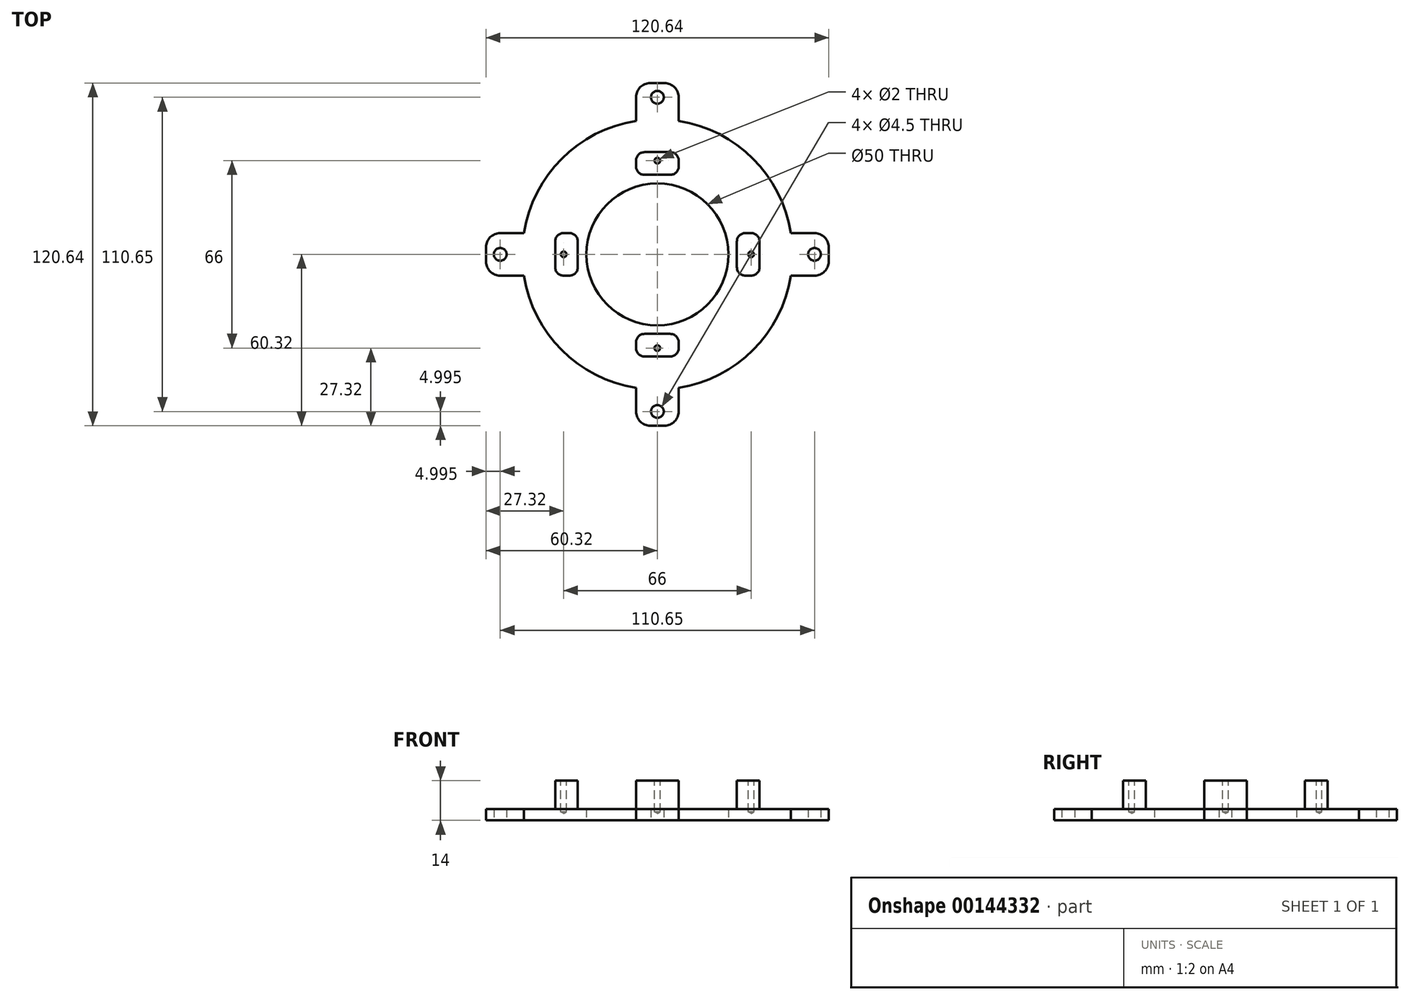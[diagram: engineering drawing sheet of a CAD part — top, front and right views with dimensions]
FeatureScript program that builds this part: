
annotation { "Feature Type Name" : "Feature", "Feature Type Description" : "" }
export const myFeature = defineFeature(function(context is Context, id is Id, definition is map)
    precondition{}
    {
        {
            var Q0;
            Q0=qCreatedBy(makeId("Top.planeOp"),FACE);
            var sketch = newSketch(context, id + "F0", { "sketchPlane" : qUnion([Q0])});
            skCircle(sketch, "E0", {"center": v(0, 0) * mm, "radius": 25 * mm});
            skCircle(sketch, "E1", {"center": v(0, 0) * mm, "radius": 47.63 * mm});
            skLineSegment(sketch, "E2", {"start": v(0, 47.63) * mm, "end": v(0, -47.63) * mm});
            skLineSegment(sketch, "E3", {"start": v(47.63, 0) * mm, "end": v(-47.63, 0) * mm});
            skLineSegment(sketch, "E4.bottom", {"start": v(7.5, 36) * mm, "end": v(-7.5, 36) * mm});
            skLineSegment(sketch, "E4.top", {"start": v(7.5, 28) * mm, "end": v(-7.5, 28) * mm});
            skLineSegment(sketch, "E4.left", {"start": v(7.5, 36) * mm, "end": v(7.5, 28) * mm});
            skLineSegment(sketch, "E4.right", {"start": v(-7.5, 36) * mm, "end": v(-7.5, 28) * mm});
            skPoint(sketch, "E5", {"position": v(0, 36) * mm});
            skPoint(sketch, "E6", {"position": v(0, 33) * mm});
            skLineSegment(sketch, "E7.bottom", {"start": v(-36, 7.5) * mm, "end": v(-28, 7.5) * mm});
            skLineSegment(sketch, "E7.top", {"start": v(-36, -7.5) * mm, "end": v(-28, -7.5) * mm});
            skLineSegment(sketch, "E7.left", {"start": v(-36, 7.5) * mm, "end": v(-36, -7.5) * mm});
            skLineSegment(sketch, "E7.right", {"start": v(-28, 7.5) * mm, "end": v(-28, -7.5) * mm});
            skLineSegment(sketch, "E8.bottom", {"start": v(36, 7.5) * mm, "end": v(28, 7.5) * mm});
            skLineSegment(sketch, "E8.top", {"start": v(36, -7.5) * mm, "end": v(28, -7.5) * mm});
            skLineSegment(sketch, "E8.left", {"start": v(36, 7.5) * mm, "end": v(36, -7.5) * mm});
            skLineSegment(sketch, "E8.right", {"start": v(28, 7.5) * mm, "end": v(28, -7.5) * mm});
            skLineSegment(sketch, "E9.bottom", {"start": v(7.5, -28) * mm, "end": v(-7.5, -28) * mm});
            skLineSegment(sketch, "E9.top", {"start": v(7.5, -36) * mm, "end": v(-7.5, -36) * mm});
            skLineSegment(sketch, "E9.left", {"start": v(7.5, -28) * mm, "end": v(7.5, -36) * mm});
            skLineSegment(sketch, "E9.right", {"start": v(-7.5, -28) * mm, "end": v(-7.5, -36) * mm});
            skPoint(sketch, "E10", {"position": v(36, 0) * mm});
            skPoint(sketch, "E11", {"position": v(-36, 0) * mm});
            skPoint(sketch, "E12", {"position": v(0, -36) * mm});
            skPoint(sketch, "E13", {"position": v(33, 0) * mm});
            skPoint(sketch, "E14", {"position": v(-33, 0) * mm});
            skPoint(sketch, "E15", {"position": v(0, -33) * mm});
            skLineSegment(sketch, "E16.bottom", {"start": v(-7.5, -36) * mm, "end": v(7.5, -36) * mm});
            skLineSegment(sketch, "E16.top", {"start": v(-7.5, -60.33) * mm, "end": v(7.5, -60.33) * mm});
            skLineSegment(sketch, "E16.left", {"start": v(-7.5, -36) * mm, "end": v(-7.5, -60.33) * mm});
            skLineSegment(sketch, "E16.right", {"start": v(7.5, -36) * mm, "end": v(7.5, -60.33) * mm});
            skLineSegment(sketch, "E17.bottom", {"start": v(-36, 7.5) * mm, "end": v(-60.33, 7.5) * mm});
            skLineSegment(sketch, "E17.top", {"start": v(-36, -7.5) * mm, "end": v(-60.33, -7.5) * mm});
            skLineSegment(sketch, "E17.right", {"start": v(-60.33, 7.5) * mm, "end": v(-60.33, -7.5) * mm});
            skLineSegment(sketch, "E18.bottom", {"start": v(-7.5, 36) * mm, "end": v(7.5, 36) * mm});
            skLineSegment(sketch, "E18.top", {"start": v(-7.5, 60.33) * mm, "end": v(7.5, 60.33) * mm});
            skLineSegment(sketch, "E18.left", {"start": v(-7.5, 36) * mm, "end": v(-7.5, 60.33) * mm});
            skLineSegment(sketch, "E18.right", {"start": v(7.5, 36) * mm, "end": v(7.5, 60.33) * mm});
            skLineSegment(sketch, "E19.bottom", {"start": v(36, 7.5) * mm, "end": v(60.33, 7.5) * mm});
            skLineSegment(sketch, "E19.top", {"start": v(36, -7.5) * mm, "end": v(60.33, -7.5) * mm});
            skLineSegment(sketch, "E19.right", {"start": v(60.33, 7.5) * mm, "end": v(60.33, -7.5) * mm});
            skPoint(sketch, "E20", {"position": v(0, 55.33) * mm});
            skPoint(sketch, "E21", {"position": v(55.33, 0) * mm});
            skPoint(sketch, "E22", {"position": v(0, -55.33) * mm});
            skPoint(sketch, "E23", {"position": v(-55.33, 0) * mm});
            skSolve(sketch);
        }
        {
            var Q0;
            Q0 = qSketchRegion(id + "F0", true);
            extrude(context, id + "F1", {"entities" : qUnion([Q0]), "depth" : 4 * mm});
        }
        {
            var Q0;
            {var subQ5=sQuery(id+"F0.wireOp",EDGE,"E4.left");Q0=makeQuery(id+"F0.imprint","IMPRINT",FACE,{"disambiguationData":[TD([[makeQuery(id+"F0.imprint","IMPRINT",EDGE,{"derivedFrom":subQ5}),-1.0]])]});}
            var Q1;
            {var subQ5=sQuery(id+"F0.wireOp",EDGE,"E4.right");Q1=makeQuery(id+"F0.imprint","IMPRINT",FACE,{"disambiguationData":[TD([[makeQuery(id+"F0.imprint","IMPRINT",EDGE,{"derivedFrom":subQ5}),1.0]])]});}
            var Q2;
            {var subQ5=sQuery(id+"F0.wireOp",EDGE,"E8.bottom");Q2=makeQuery(id+"F0.imprint","IMPRINT",FACE,{"disambiguationData":[TD([[makeQuery(id+"F0.imprint","IMPRINT",EDGE,{"derivedFrom":subQ5}),1.0]])]});}
            var Q3;
            {var subQ5=sQuery(id+"F0.wireOp",EDGE,"E8.top");Q3=makeQuery(id+"F0.imprint","IMPRINT",FACE,{"disambiguationData":[TD([[makeQuery(id+"F0.imprint","IMPRINT",EDGE,{"derivedFrom":subQ5}),-1.0]])]});}
            var Q4;
            {var subQ5=sQuery(id+"F0.wireOp",EDGE,"E9.left");Q4=makeQuery(id+"F0.imprint","IMPRINT",FACE,{"disambiguationData":[TD([[makeQuery(id+"F0.imprint","IMPRINT",EDGE,{"derivedFrom":subQ5}),-1.0]])]});}
            var Q5;
            {var subQ5=sQuery(id+"F0.wireOp",EDGE,"E9.right");Q5=makeQuery(id+"F0.imprint","IMPRINT",FACE,{"disambiguationData":[TD([[makeQuery(id+"F0.imprint","IMPRINT",EDGE,{"derivedFrom":subQ5}),1.0]])]});}
            var Q6;
            {var subQ5=sQuery(id+"F0.wireOp",EDGE,"E7.top");Q6=makeQuery(id+"F0.imprint","IMPRINT",FACE,{"disambiguationData":[TD([[makeQuery(id+"F0.imprint","IMPRINT",EDGE,{"derivedFrom":subQ5}),1.0]])]});}
            var Q7;
            {var subQ5=sQuery(id+"F0.wireOp",EDGE,"E7.bottom");Q7=makeQuery(id+"F0.imprint","IMPRINT",FACE,{"disambiguationData":[TD([[makeQuery(id+"F0.imprint","IMPRINT",EDGE,{"derivedFrom":subQ5}),-1.0]])]});}
            extrude(context, id + "F2", {"entities" : qUnion([Q0, Q1, Q2, Q3, Q4, Q5, Q6, Q7]), "operationType" : NewBodyOperationType.ADD, "depth" : 14 * mm});
        }
        {
            var Q0;
            Q0=makeQuery(id+"F2.opExtrude","CAP_FACE",FACE,{"disambiguationData":[OSD([sQuery(id+"F0.wireOp",EDGE,"E4.bottom"),sQuery(id+"F0.wireOp",EDGE,"E4.top"),sQuery(id+"F0.wireOp",EDGE,"E4.left"),sQuery(id+"F0.wireOp",EDGE,"E4.right")])],"isStart":false});
            var sketch = newSketch(context, id + "F3", { "sketchPlane" : qUnion([Q0])});
            skPoint(sketch, "E24", {"position": v(0, 33) * mm});
            skPoint(sketch, "E24.positionSnap0", {"position": v(0, 36) * mm});
            skPoint(sketch, "E25", {"position": v(-33, 0) * mm});
            skPoint(sketch, "E26", {"position": v(0, -33) * mm});
            skPoint(sketch, "E27", {"position": v(33, 0) * mm});
            skSolve(sketch);
        }
        {
            var Q0;
            Q0=sQuery(id+"F3.wireOp",VERTEX,"E24");
            var Q1;
            Q1=sQuery(id+"F3.wireOp",VERTEX,"E27");
            var Q2;
            Q2=sQuery(id+"F3.wireOp",VERTEX,"E26");
            var Q3;
            Q3=sQuery(id+"F3.wireOp",VERTEX,"E25");
            var Q4;
            Q4=makeQuery(id+"F1.opExtrude","SWEPT_BODY",BODY,{"disambiguationData":[OSD([sQuery(id+"F0.wireOp",EDGE,"E0"),sQuery(id+"F0.wireOp",EDGE,"E1"),sQuery(id+"F0.wireOp",EDGE,"E4.bottom"),sQuery(id+"F0.wireOp",EDGE,"E4.top"),sQuery(id+"F0.wireOp",EDGE,"E4.left"),sQuery(id+"F0.wireOp",EDGE,"E4.right"),sQuery(id+"F0.wireOp",EDGE,"E7.bottom"),sQuery(id+"F0.wireOp",EDGE,"E7.top"),sQuery(id+"F0.wireOp",EDGE,"E7.left"),sQuery(id+"F0.wireOp",EDGE,"E7.right"),sQuery(id+"F0.wireOp",EDGE,"E8.bottom"),sQuery(id+"F0.wireOp",EDGE,"E8.top"),sQuery(id+"F0.wireOp",EDGE,"E8.left"),sQuery(id+"F0.wireOp",EDGE,"E8.right"),sQuery(id+"F0.wireOp",EDGE,"E9.bottom"),sQuery(id+"F0.wireOp",EDGE,"E9.top"),sQuery(id+"F0.wireOp",EDGE,"E9.left"),sQuery(id+"F0.wireOp",EDGE,"E9.right")])]});
            hole(context, id + "F4", {"style" : HoleStyle.SIMPLE, "endStyle" : HoleEndStyle.BLIND, "holeDiameter" : 2 * mm, "holeDepth" : 11 * mm, "locations" : qUnion([Q0, Q1, Q2, Q3]), "scope" : qUnion([Q4])});
        }
        {
            var Q0;
            Q0=sQuery(id+"F0.wireOp",VERTEX,"E20");
            var Q1;
            Q1=sQuery(id+"F0.wireOp",VERTEX,"E21");
            var Q2;
            Q2=sQuery(id+"F0.wireOp",VERTEX,"E22");
            var Q3;
            Q3=sQuery(id+"F0.wireOp",VERTEX,"E23");
            var Q4;
            Q4=makeQuery(id+"F1.opExtrude","SWEPT_BODY",BODY,{"disambiguationData":[OSD([sQuery(id+"F0.wireOp",EDGE,"E0"),sQuery(id+"F0.wireOp",EDGE,"E1"),sQuery(id+"F0.wireOp",EDGE,"E4.top"),sQuery(id+"F0.wireOp",EDGE,"E4.left"),sQuery(id+"F0.wireOp",EDGE,"E4.right"),sQuery(id+"F0.wireOp",EDGE,"E7.bottom"),sQuery(id+"F0.wireOp",EDGE,"E7.top"),sQuery(id+"F0.wireOp",EDGE,"E7.right"),sQuery(id+"F0.wireOp",EDGE,"E8.bottom"),sQuery(id+"F0.wireOp",EDGE,"E8.top"),sQuery(id+"F0.wireOp",EDGE,"E8.right"),sQuery(id+"F0.wireOp",EDGE,"E9.bottom"),sQuery(id+"F0.wireOp",EDGE,"E9.left"),sQuery(id+"F0.wireOp",EDGE,"E9.right"),sQuery(id+"F0.wireOp",EDGE,"E16.bottom"),sQuery(id+"F0.wireOp",EDGE,"E16.top"),sQuery(id+"F0.wireOp",EDGE,"E16.left"),sQuery(id+"F0.wireOp",EDGE,"E16.right"),sQuery(id+"F0.wireOp",EDGE,"E17.bottom"),sQuery(id+"F0.wireOp",EDGE,"E17.top"),sQuery(id+"F0.wireOp",EDGE,"E7.left"),sQuery(id+"F0.wireOp",EDGE,"E17.right"),sQuery(id+"F0.wireOp",EDGE,"E18.bottom"),sQuery(id+"F0.wireOp",EDGE,"E18.top"),sQuery(id+"F0.wireOp",EDGE,"E18.left"),sQuery(id+"F0.wireOp",EDGE,"E18.right"),sQuery(id+"F0.wireOp",EDGE,"E19.bottom"),sQuery(id+"F0.wireOp",EDGE,"E19.top"),sQuery(id+"F0.wireOp",EDGE,"E8.left"),sQuery(id+"F0.wireOp",EDGE,"E19.right")])]});
            hole(context, id + "F5", {"style" : HoleStyle.SIMPLE, "endStyle" : HoleEndStyle.BLIND, "oppositeDirection" : true, "holeDiameter" : 4.5 * mm, "holeDepth" : 11 * mm, "locations" : qUnion([Q0, Q1, Q2, Q3]), "scope" : qUnion([Q4])});
        }
        {
            var Q0;
            Q0=makeQuery(id+"F1.opExtrude","SWEPT_EDGE",EDGE,{"disambiguationData":[OSD([sQuery(id+"F0.wireOp",EDGE,"E18.top"),sQuery(id+"F0.wireOp",EDGE,"E18.right")])]});
            var Q1;
            Q1=makeQuery(id+"F1.opExtrude","SWEPT_EDGE",EDGE,{"disambiguationData":[OSD([sQuery(id+"F0.wireOp",EDGE,"E18.top"),sQuery(id+"F0.wireOp",EDGE,"E18.left")])]});
            var Q2;
            Q2=makeQuery(id+"F1.opExtrude","SWEPT_EDGE",EDGE,{"disambiguationData":[OSD([sQuery(id+"F0.wireOp",EDGE,"E17.bottom"),sQuery(id+"F0.wireOp",EDGE,"E17.right")])]});
            var Q3;
            Q3=makeQuery(id+"F1.opExtrude","SWEPT_EDGE",EDGE,{"disambiguationData":[OSD([sQuery(id+"F0.wireOp",EDGE,"E17.top"),sQuery(id+"F0.wireOp",EDGE,"E17.right")])]});
            var Q4;
            Q4=makeQuery(id+"F1.opExtrude","SWEPT_EDGE",EDGE,{"disambiguationData":[OSD([sQuery(id+"F0.wireOp",EDGE,"E16.top"),sQuery(id+"F0.wireOp",EDGE,"E16.right")])]});
            var Q5;
            Q5=makeQuery(id+"F1.opExtrude","SWEPT_EDGE",EDGE,{"disambiguationData":[OSD([sQuery(id+"F0.wireOp",EDGE,"E16.top"),sQuery(id+"F0.wireOp",EDGE,"E16.left")])]});
            var Q6;
            Q6=makeQuery(id+"F1.opExtrude","SWEPT_EDGE",EDGE,{"disambiguationData":[OSD([sQuery(id+"F0.wireOp",EDGE,"E19.top"),sQuery(id+"F0.wireOp",EDGE,"E19.right")])]});
            var Q7;
            Q7=makeQuery(id+"F1.opExtrude","SWEPT_EDGE",EDGE,{"disambiguationData":[OSD([sQuery(id+"F0.wireOp",EDGE,"E19.bottom"),sQuery(id+"F0.wireOp",EDGE,"E19.right")])]});
            fillet(context, id + "F6", {"entities" : qUnion([Q0, Q1, Q2, Q3, Q4, Q5, Q6, Q7]), "radius" : 5 * mm, "tangentPropagation" : true, "allowEdgeOverflow" : false});
        }
        {
            var Q0;
            Q0=makeQuery(id+"F2.opExtrude","SWEPT_EDGE",EDGE,{"disambiguationData":[OSD([sQuery(id+"F0.wireOp",EDGE,"E4.top"),sQuery(id+"F0.wireOp",EDGE,"E4.left")])]});
            var Q1;
            Q1=makeQuery(id+"F2.opExtrude","SWEPT_EDGE",EDGE,{"disambiguationData":[OSD([sQuery(id+"F0.wireOp",EDGE,"E4.left"),sQuery(id+"F0.wireOp",EDGE,"E18.bottom"),sQuery(id+"F0.wireOp",EDGE,"E18.right")])]});
            var Q2;
            Q2=makeQuery(id+"F2.opExtrude","SWEPT_EDGE",EDGE,{"disambiguationData":[OSD([sQuery(id+"F0.wireOp",EDGE,"E4.top"),sQuery(id+"F0.wireOp",EDGE,"E4.right")])]});
            var Q3;
            Q3=makeQuery(id+"F2.opExtrude","SWEPT_EDGE",EDGE,{"disambiguationData":[OSD([sQuery(id+"F0.wireOp",EDGE,"E4.right"),sQuery(id+"F0.wireOp",EDGE,"E18.bottom"),sQuery(id+"F0.wireOp",EDGE,"E18.left")])]});
            var Q4;
            Q4=makeQuery(id+"F2.opExtrude","SWEPT_EDGE",EDGE,{"disambiguationData":[OSD([sQuery(id+"F0.wireOp",EDGE,"E7.top"),sQuery(id+"F0.wireOp",EDGE,"E17.top"),sQuery(id+"F0.wireOp",EDGE,"E7.left")])]});
            var Q5;
            Q5=makeQuery(id+"F2.opExtrude","SWEPT_EDGE",EDGE,{"disambiguationData":[OSD([sQuery(id+"F0.wireOp",EDGE,"E7.top"),sQuery(id+"F0.wireOp",EDGE,"E7.right")])]});
            var Q6;
            Q6=makeQuery(id+"F2.opExtrude","SWEPT_EDGE",EDGE,{"disambiguationData":[OSD([sQuery(id+"F0.wireOp",EDGE,"E7.bottom"),sQuery(id+"F0.wireOp",EDGE,"E17.bottom"),sQuery(id+"F0.wireOp",EDGE,"E7.left")])]});
            var Q7;
            Q7=makeQuery(id+"F2.opExtrude","SWEPT_EDGE",EDGE,{"disambiguationData":[OSD([sQuery(id+"F0.wireOp",EDGE,"E7.bottom"),sQuery(id+"F0.wireOp",EDGE,"E7.right")])]});
            var Q8;
            Q8=makeQuery(id+"F2.opExtrude","SWEPT_EDGE",EDGE,{"disambiguationData":[OSD([sQuery(id+"F0.wireOp",EDGE,"E9.bottom"),sQuery(id+"F0.wireOp",EDGE,"E9.right")])]});
            var Q9;
            Q9=makeQuery(id+"F2.opExtrude","SWEPT_EDGE",EDGE,{"disambiguationData":[OSD([sQuery(id+"F0.wireOp",EDGE,"E9.bottom"),sQuery(id+"F0.wireOp",EDGE,"E9.left")])]});
            var Q10;
            Q10=makeQuery(id+"F2.opExtrude","SWEPT_EDGE",EDGE,{"disambiguationData":[OSD([sQuery(id+"F0.wireOp",EDGE,"E8.bottom"),sQuery(id+"F0.wireOp",EDGE,"E19.bottom"),sQuery(id+"F0.wireOp",EDGE,"E8.left")])]});
            var Q11;
            Q11=makeQuery(id+"F2.opExtrude","SWEPT_EDGE",EDGE,{"disambiguationData":[OSD([sQuery(id+"F0.wireOp",EDGE,"E8.bottom"),sQuery(id+"F0.wireOp",EDGE,"E8.right")])]});
            var Q12;
            Q12=makeQuery(id+"F2.opExtrude","SWEPT_EDGE",EDGE,{"disambiguationData":[OSD([sQuery(id+"F0.wireOp",EDGE,"E8.top"),sQuery(id+"F0.wireOp",EDGE,"E19.top"),sQuery(id+"F0.wireOp",EDGE,"E8.left")])]});
            var Q13;
            Q13=makeQuery(id+"F2.opExtrude","SWEPT_EDGE",EDGE,{"disambiguationData":[OSD([sQuery(id+"F0.wireOp",EDGE,"E8.top"),sQuery(id+"F0.wireOp",EDGE,"E8.right")])]});
            var Q14;
            Q14=makeQuery(id+"F2.opExtrude","SWEPT_EDGE",EDGE,{"disambiguationData":[OSD([sQuery(id+"F0.wireOp",EDGE,"E9.left"),sQuery(id+"F0.wireOp",EDGE,"E16.bottom"),sQuery(id+"F0.wireOp",EDGE,"E16.right")])]});
            var Q15;
            Q15=makeQuery(id+"F2.opExtrude","SWEPT_EDGE",EDGE,{"disambiguationData":[OSD([sQuery(id+"F0.wireOp",EDGE,"E9.right"),sQuery(id+"F0.wireOp",EDGE,"E16.bottom"),sQuery(id+"F0.wireOp",EDGE,"E16.left")])]});
            fillet(context, id + "F7", {"entities" : qUnion([Q0, Q1, Q2, Q3, Q4, Q5, Q6, Q7, Q8, Q9, Q10, Q11, Q12, Q13, Q14, Q15]), "radius" : 3 * mm, "tangentPropagation" : true, "allowEdgeOverflow" : false});
        }
    });
